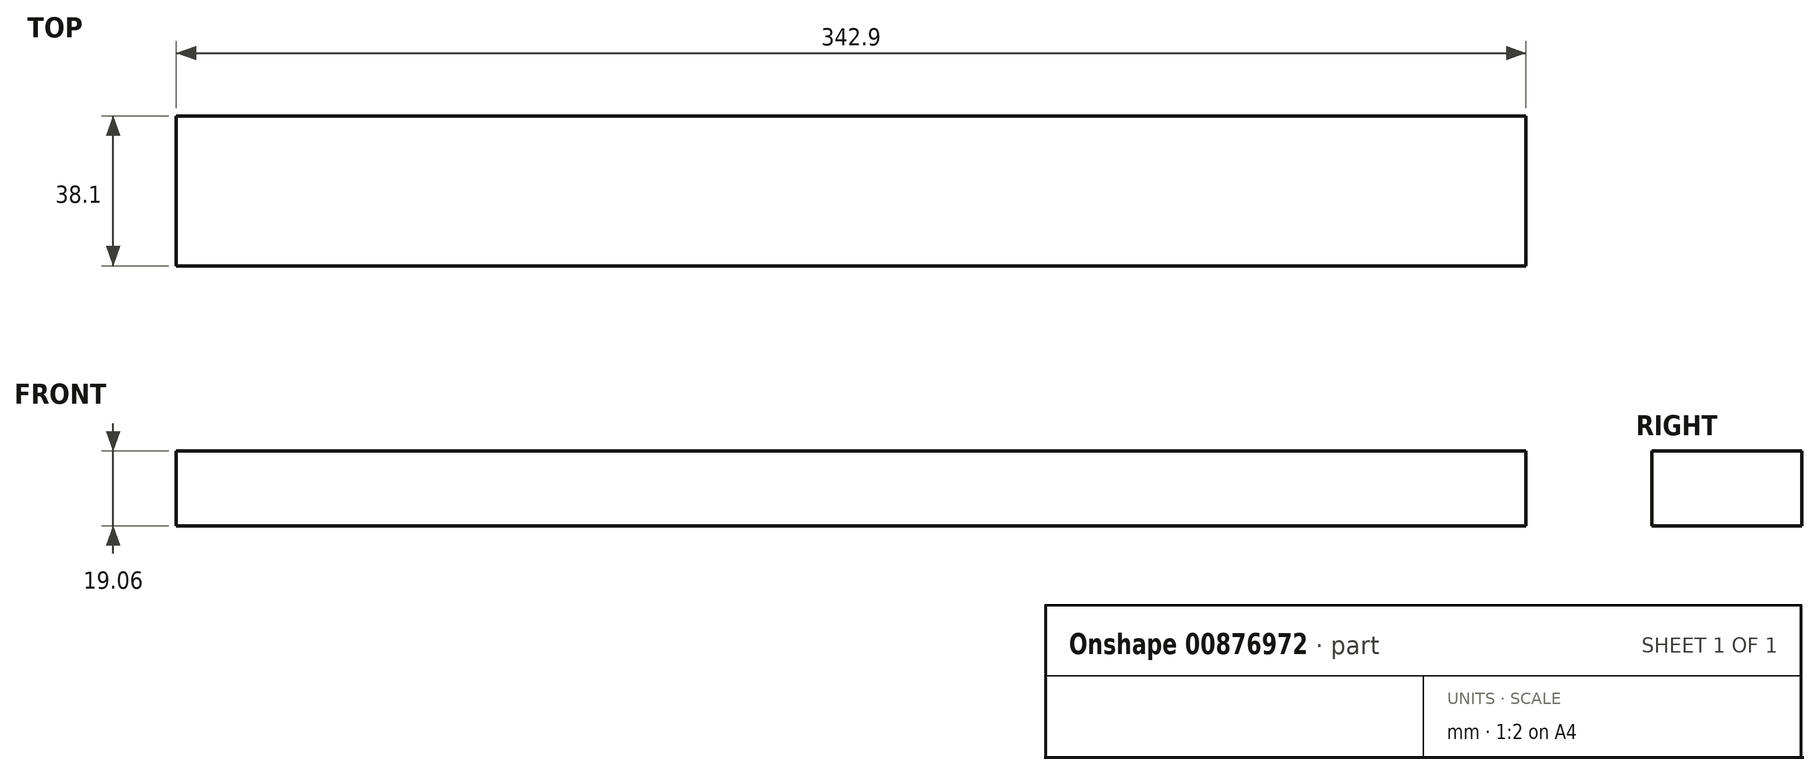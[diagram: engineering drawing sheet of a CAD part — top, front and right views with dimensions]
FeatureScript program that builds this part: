
annotation { "Feature Type Name" : "Feature", "Feature Type Description" : "" }
export const myFeature = defineFeature(function(context is Context, id is Id, definition is map)
    precondition{}
    {
        {
            var Q0;
            Q0=qCreatedBy(makeId("Right.planeOp"),FACE);
            var sketch = newSketch(context, id + "F0", { "sketchPlane" : qUnion([Q0])});
            skLineSegment(sketch, "E0.bottom", {"start": v(19.05, 9.53) * mm, "end": v(-19.05, 9.53) * mm});
            skLineSegment(sketch, "E0.top", {"start": v(19.05, -9.53) * mm, "end": v(-19.05, -9.53) * mm});
            skLineSegment(sketch, "E0.left", {"start": v(19.05, 9.53) * mm, "end": v(19.05, -9.53) * mm});
            skLineSegment(sketch, "E0.right", {"start": v(-19.05, 9.53) * mm, "end": v(-19.05, -9.53) * mm});
            skPoint(sketch, "E0.middle", {"position": v(0, 0) * mm});
            skSolve(sketch);
        }
        {
            var Q0;
            Q0=makeQuery(id+"F0.imprint","IMPRINT",FACE,{"disambiguationData":[TD([[makeQuery(id+"F0.imprint","IMPRINT",EDGE,{"derivedFrom":sQuery(id+"F0.wireOp",EDGE,"E0.bottom")}),1.0]])]});
            extrude(context, id + "F1", {"entities" : qUnion([Q0]), "depth" : 342.9 * mm, "offsetDistance" : 25.4 * mm});
        }
    });
